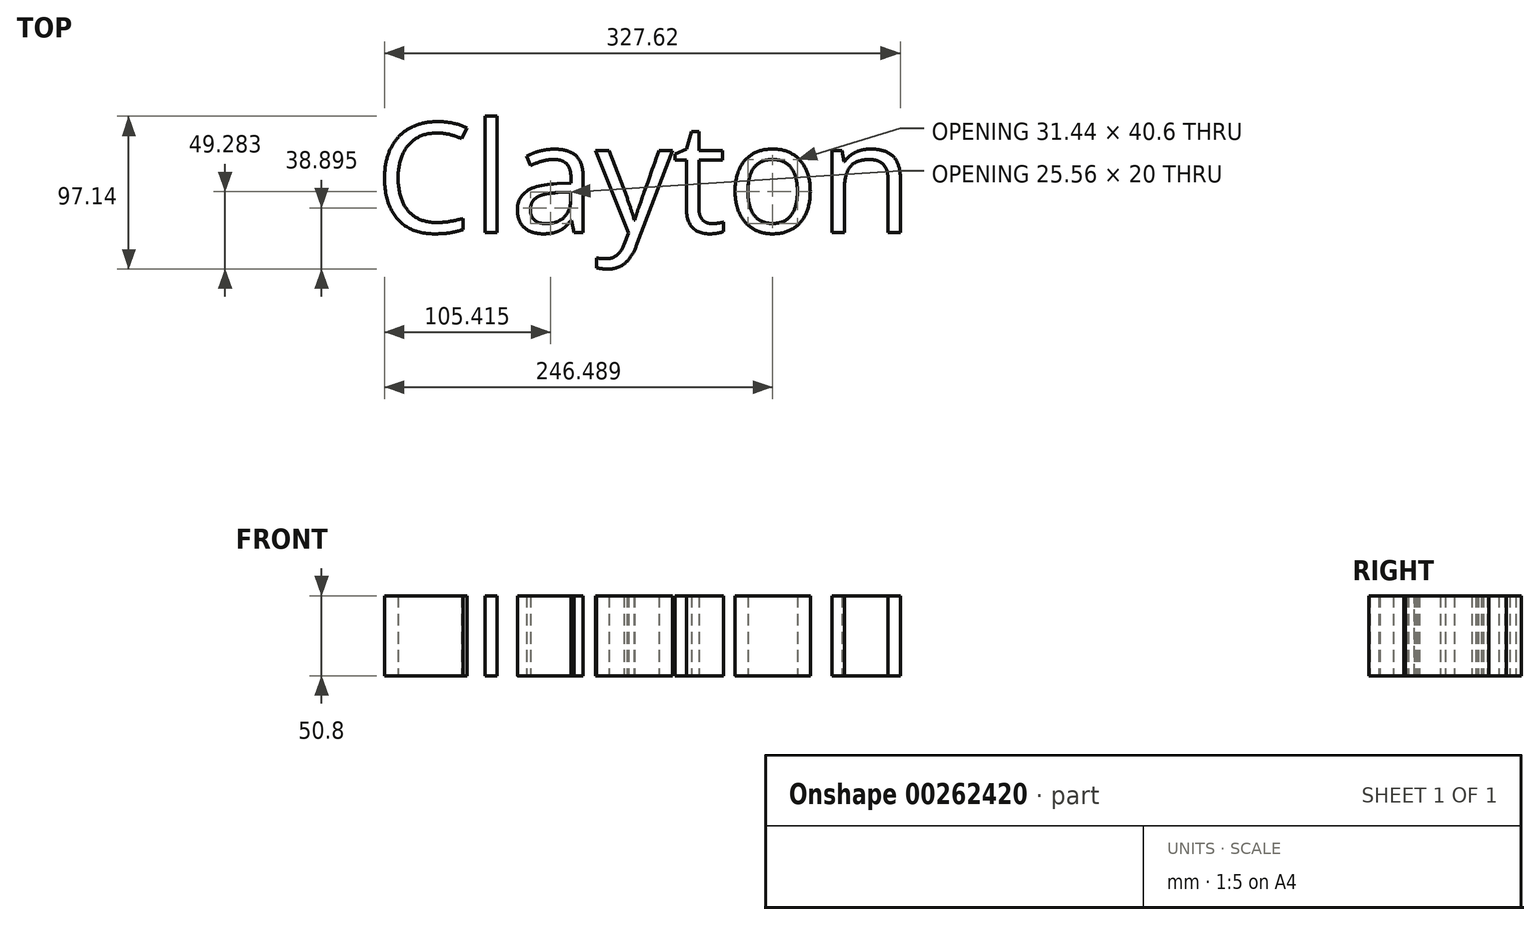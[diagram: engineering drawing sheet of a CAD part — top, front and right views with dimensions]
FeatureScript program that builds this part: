
annotation { "Feature Type Name" : "Feature", "Feature Type Description" : "" }
export const myFeature = defineFeature(function(context is Context, id is Id, definition is map)
    precondition{}
    {
        {
            var Q0;
            Q0=qCreatedBy(makeId("Top.planeOp"),FACE);
            var sketch = newSketch(context, id + "F0", { "sketchPlane" : qUnion([Q0])});
            skText(sketch, "E0", { "text": "Clayton\n", "fontName": "OpenSans-Regular.ttf"});
            const initialGuessF0  = {"E0": [-0.13948, -0.08198, 1, 0, 0.06993]};
            skSetInitialGuess(sketch, initialGuessF0);
            skSolve(sketch);
        }
        {
            var Q0;
            Q0 = qSketchRegion(id + "F0", true);
            extrude(context, id + "F1", {"entities" : qUnion([Q0]), "depth" : 50.8 * mm});
        }
    });
